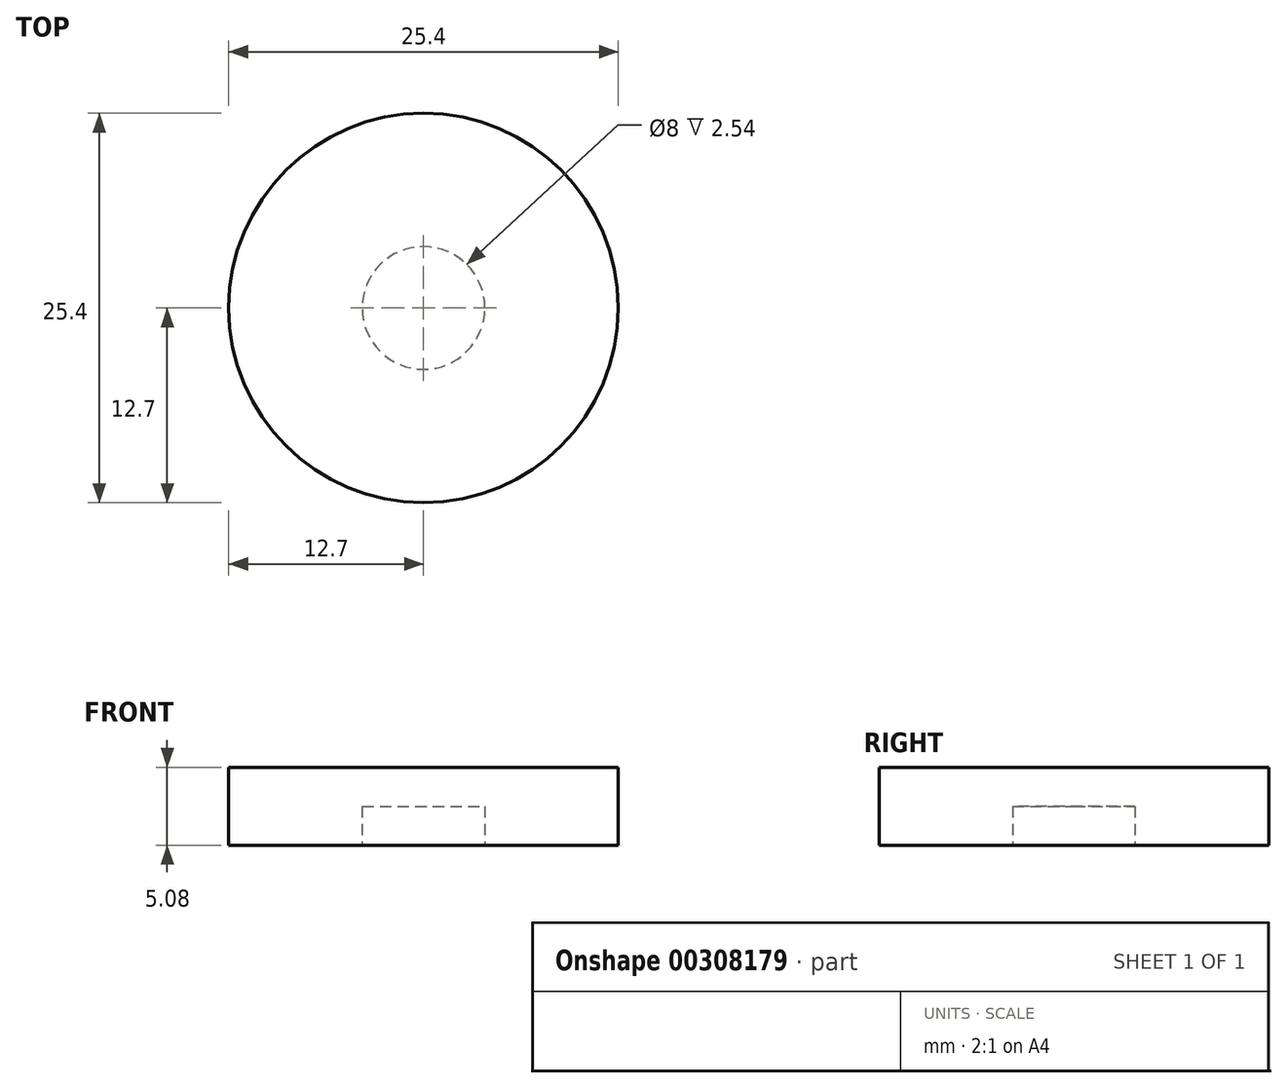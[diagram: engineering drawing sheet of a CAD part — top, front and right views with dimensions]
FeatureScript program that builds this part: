
annotation { "Feature Type Name" : "Feature", "Feature Type Description" : "" }
export const myFeature = defineFeature(function(context is Context, id is Id, definition is map)
    precondition{}
    {
        {
            var Q0;
            Q0=qCreatedBy(makeId("Top.planeOp"),FACE);
            var sketch = newSketch(context, id + "F0", { "sketchPlane" : qUnion([Q0])});
            skCircle(sketch, "E0", {"center": v(0, 0) * mm, "radius": 4 * mm});
            skCircle(sketch, "E1", {"center": v(0, 0) * mm, "radius": 12.7 * mm});
            skSolve(sketch);
        }
        {
            var Q0;
            Q0 = qSketchRegion(id + "F0", true);
            var Q1;
            Q1=makeQuery(id+"F0.imprint","IMPRINT",FACE,{"disambiguationData":[TD([[makeQuery(id+"F0.imprint","IMPRINT",EDGE,{"derivedFrom":sQuery(id+"F0.wireOp",EDGE,"E0")}),1.0]])]});
            extrude(context, id + "F1", {"entities" : qUnion([Q0, Q1]), "depth" : 5.08 * mm});
        }
        {
            var Q0;
            Q0=makeQuery(id+"F1.opExtrude","CAP_FACE",FACE,{"disambiguationData":[OSD([sQuery(id+"F0.wireOp",EDGE,"E1")])],"isStart":true});
            var sketch = newSketch(context, id + "F2", { "sketchPlane" : qUnion([Q0])});
            skCircle(sketch, "E2", {"center": v(0, 0) * mm, "radius": 4 * mm});
            skSolve(sketch);
        }
        {
            var Q0;
            Q0=makeQuery(id+"F2.imprint","IMPRINT",FACE,{"disambiguationData":[TD([[makeQuery(id+"F2.imprint","IMPRINT",EDGE,{"derivedFrom":sQuery(id+"F2.wireOp",EDGE,"E2")}),1.0]])]});
            extrude(context, id + "F3", {"entities" : qUnion([Q0]), "operationType" : NewBodyOperationType.REMOVE, "oppositeDirection" : true, "depth" : 2.54 * mm});
        }
    });
